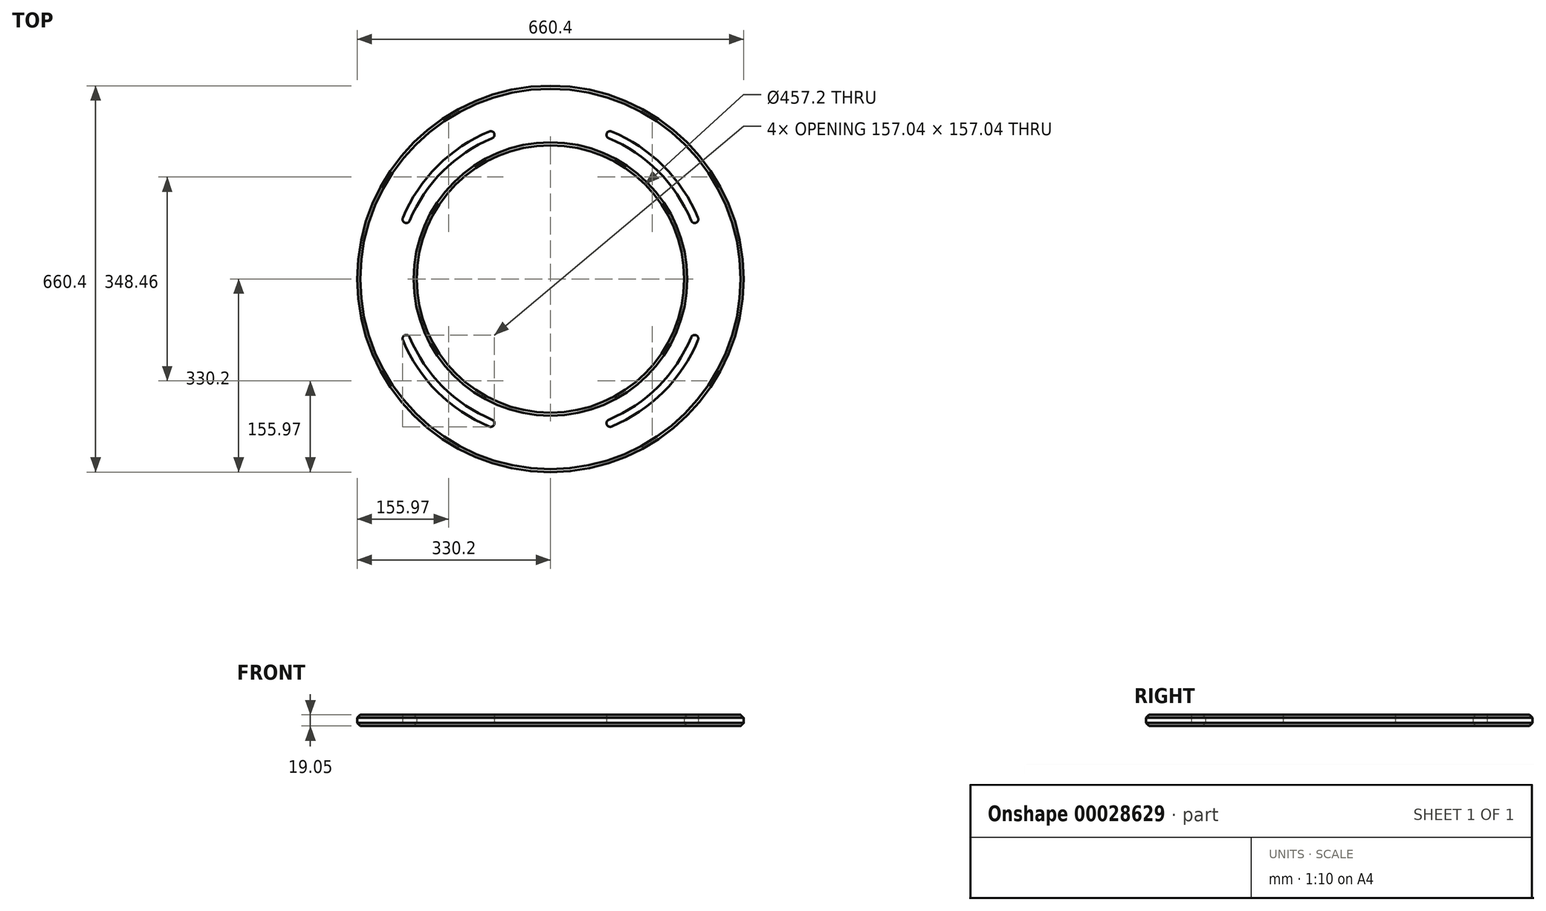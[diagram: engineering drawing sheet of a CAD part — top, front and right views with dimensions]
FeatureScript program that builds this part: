
annotation { "Feature Type Name" : "Feature", "Feature Type Description" : "" }
export const myFeature = defineFeature(function(context is Context, id is Id, definition is map)
    precondition{}
    {
        {
            var Q0;
            Q0=qCreatedBy(makeId("Top.planeOp"),FACE);
            var sketch = newSketch(context, id + "F0", { "sketchPlane" : qUnion([Q0])});
            skCircle(sketch, "E0", {"center": v(0, 0) * mm, "radius": 228.6 * mm});
            skCircle(sketch, "E1", {"center": v(0, 0) * mm, "radius": 330.2 * mm});
            skArc(sketch, "E2", {"start": v(-102.06, 246.4) * mm, "mid": v(-188.59, 188.59) * mm, "end": v(-246.4, 102.06) * mm, "construction": true});
            skLineSegment(sketch, "E3", {"start": v(-330.2, 0) * mm, "end": v(330.2, 0) * mm, "construction": true});
            skLineSegment(sketch, "E4", {"start": v(0, 330.2) * mm, "end": v(0, -330.2) * mm, "construction": true});
            skLineSegment(sketch, "E5", {"start": v(-126.36, 305.07) * mm, "end": v(0, 0) * mm, "construction": true});
            skLineSegment(sketch, "E6", {"start": v(0, 0) * mm, "end": v(-305.07, 126.36) * mm, "construction": true});
            skLineSegment(sketch, "E7", {"start": v(0, 0) * mm, "end": v(126.36, 305.07) * mm, "construction": true});
            skLineSegment(sketch, "E8", {"start": v(0, 0) * mm, "end": v(305.07, 126.36) * mm, "construction": true});
            skLineSegment(sketch, "E9", {"start": v(0, 0) * mm, "end": v(305.07, -126.36) * mm, "construction": true});
            skLineSegment(sketch, "E10", {"start": v(0, 0) * mm, "end": v(126.36, -305.07) * mm, "construction": true});
            skLineSegment(sketch, "E11", {"start": v(0, 0) * mm, "end": v(-126.36, -305.07) * mm, "construction": true});
            skLineSegment(sketch, "E12", {"start": v(0, 0) * mm, "end": v(-305.07, -126.36) * mm, "construction": true});
            skArc(sketch, "E13.trimOffspring", {"start": v(246.4, 102.06) * mm, "mid": v(188.59, 188.59) * mm, "end": v(102.06, 246.4) * mm, "construction": true});
            skArc(sketch, "E14.trimOffspring", {"start": v(102.06, -246.4) * mm, "mid": v(188.59, -188.59) * mm, "end": v(246.4, -102.06) * mm, "construction": true});
            skArc(sketch, "E15.trimOffspring", {"start": v(-246.4, -102.06) * mm, "mid": v(-188.59, -188.59) * mm, "end": v(-102.06, -246.4) * mm, "construction": true});
            skArc(sketch, "E16.0.startCap", {"start": v(-104.5, 252.27) * mm, "mid": v(-96.2, 248.83) * mm, "end": v(-99.63, 240.53) * mm});
            skArc(sketch, "E16.0.endCap", {"start": v(-240.53, 99.63) * mm, "mid": v(-248.83, 96.2) * mm, "end": v(-252.27, 104.5) * mm});
            skArc(sketch, "E16.0.left", {"start": v(-99.63, 240.53) * mm, "mid": v(-184.1, 184.1) * mm, "end": v(-240.53, 99.63) * mm});
            skArc(sketch, "E16.0.right", {"start": v(-104.5, 252.27) * mm, "mid": v(-193.08, 193.08) * mm, "end": v(-252.27, 104.5) * mm});
            skArc(sketch, "E16.1.startCap", {"start": v(252.27, 104.5) * mm, "mid": v(248.83, 96.2) * mm, "end": v(240.53, 99.63) * mm});
            skArc(sketch, "E16.1.endCap", {"start": v(99.63, 240.53) * mm, "mid": v(96.2, 248.83) * mm, "end": v(104.5, 252.27) * mm});
            skArc(sketch, "E16.1.left", {"start": v(240.53, 99.63) * mm, "mid": v(184.1, 184.1) * mm, "end": v(99.63, 240.53) * mm});
            skArc(sketch, "E16.1.right", {"start": v(252.27, 104.5) * mm, "mid": v(193.08, 193.08) * mm, "end": v(104.5, 252.27) * mm});
            skArc(sketch, "E16.2.startCap", {"start": v(104.5, -252.27) * mm, "mid": v(96.2, -248.83) * mm, "end": v(99.63, -240.53) * mm});
            skArc(sketch, "E16.2.endCap", {"start": v(240.53, -99.63) * mm, "mid": v(248.83, -96.2) * mm, "end": v(252.27, -104.5) * mm});
            skArc(sketch, "E16.2.left", {"start": v(99.63, -240.53) * mm, "mid": v(184.1, -184.1) * mm, "end": v(240.53, -99.63) * mm});
            skArc(sketch, "E16.2.right", {"start": v(104.5, -252.27) * mm, "mid": v(193.08, -193.08) * mm, "end": v(252.27, -104.5) * mm});
            skArc(sketch, "E16.3.startCap", {"start": v(-252.27, -104.5) * mm, "mid": v(-248.83, -96.2) * mm, "end": v(-240.53, -99.63) * mm});
            skArc(sketch, "E16.3.endCap", {"start": v(-99.63, -240.53) * mm, "mid": v(-96.2, -248.83) * mm, "end": v(-104.5, -252.27) * mm});
            skArc(sketch, "E16.3.left", {"start": v(-240.53, -99.63) * mm, "mid": v(-184.1, -184.1) * mm, "end": v(-99.63, -240.53) * mm});
            skArc(sketch, "E16.3.right", {"start": v(-252.27, -104.5) * mm, "mid": v(-193.08, -193.08) * mm, "end": v(-104.5, -252.27) * mm});
            skSolve(sketch);
        }
        {
            var Q0;
            Q0 = qSketchRegion(id + "F0", true);
            extrude(context, id + "F1", {"entities" : qUnion([Q0]), "depth" : 19.05 * mm});
        }
        {
            var Q0;
            Q0=makeQuery(id+"F1.opExtrude","CAP_EDGE",EDGE,{"disambiguationData":[OSD([sQuery(id+"F0.wireOp",EDGE,"E0")])],"isStart":false});
            var Q1;
            Q1=makeQuery(id+"F1.opExtrude","CAP_EDGE",EDGE,{"disambiguationData":[OSD([sQuery(id+"F0.wireOp",EDGE,"E1")])],"isStart":false});
            var Q2;
            Q2=makeQuery(id+"F1.opExtrude","CAP_EDGE",EDGE,{"disambiguationData":[OSD([sQuery(id+"F0.wireOp",EDGE,"E1")])],"isStart":true});
            var Q3;
            Q3=makeQuery(id+"F1.opExtrude","CAP_EDGE",EDGE,{"disambiguationData":[OSD([sQuery(id+"F0.wireOp",EDGE,"E0")])],"isStart":true});
            chamfer(context, id + "F2", {"entities" : qUnion([Q0, Q1, Q2, Q3]), "width" : 5.08 * mm, "tangentPropagation" : true});
        }
    });
